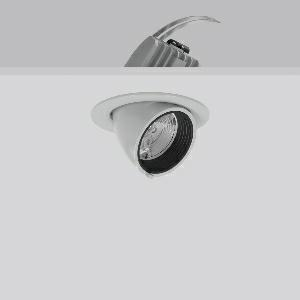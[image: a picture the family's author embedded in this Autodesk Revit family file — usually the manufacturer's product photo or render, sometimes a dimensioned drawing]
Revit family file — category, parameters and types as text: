
# Revit family: golas_mini_911573_004_76_199d
name_source: partatom
category: Lighting Fixtures
units: mm (PartAtom-declared; Revit-internal decimal feet)

## family parameters
Cut with Voids When Loaded = No
Host = Face
Light Source = No
Part Type = Normal
Room Calculation Point = No
Round Connector Dimension = Use Diameter
Shared = No

## types (1)
- GOLAS mini (1 x LED Modul 930, 1950 lm, 3000)
    Apparent Load = 20 VA
    Approval mark = CE
    CIE Flux Codes = 95 100 100 100 100
    Color Rendering = 90
    Color Temperature = 3000
    Default Elevation = 1800 mm
    Description = Series: GOLAS mini
Recessed LED projector for illuminating points to be highlighted. Housing: die-cast aluminium, powder-coated. 356° rotation range and 90° swivel range. Black plastic ring and recessed LED to prevent glare from the side. Optical assembly with lens made of plastic (polycarbonate) for the best homogeneous light distribution - can be changed without tools. Best colour rendering index Ra>90. Suitable for Recessed ceiling mounting. Installation without tools thanks to spring fastening system. Including separate LED converter with connecting cable 600 mm.High quality converter without flickering and stroboscopic effect. Through-wiring box (5 pole) available as accessory. The following accessories can be mounted without use of tools: interchangeable lenses, decorative glasses, honeycomb louvre, clear and frosted diffusers, white interchangeable plastic ring. 
Colour: silver
Diameter: 143 mm
Height: 3 mm
Cut-out diameter: 133 mm
Recess height: 170 mm
Luminaire: recess height: 115 mm
Lamp: LED
Socket: without socket
Colour temperature: 3000K
Colour rendering index (CRI): 92
System power: 20 W
Rated luminous flux: 1950 lm
Luminous efficiency: 98 lm/W
Control gear: Converter, dimmable, DALI
Protection class: II
Type of protection: IP 20
    Height = 0 mm  [stored 0 ft]
    Lamp = 1 x LED Modul 930
    Lamp Light Flux = 1950 lm
    Lamp count = 1
    Length = 143 mm
    Lifetime = 50000 h
    Luminous efficacy = 98 lm/W
    Manufacturer = RZB
    ModVariant = No
    Model = 911573.004.76
    Mounting Place = Ceiling, Wall
    Mounting Type = Recessed
    Number of Poles = 1
    OnlyDefault = Yes
    Power Factor = 1
    Product Name = GOLAS mini
    Product group = Recessed projectors
    ProductGroupID = 401
    Protection Class = Protection class II
    Protection Degree = IP 20
    RLX_Detail_Level = 1
    RLX_Emergency_Light_Flux = 0 lm
    RLX_Emergency_Type = 0
    RLX_Emergency_Type_DB = No
    RlxData = <blob elided: 53413 chars, md5=85e48752>
    Socket = socket
    Standby Power = 0 W
    System Light Flux = 1950 lm
    System Power = 20 W
    Type Comments = Product without accessories
    Type Image = 911438.004.jpg
    URL = http://relux.com
    VarID = ---
    Voltage = 230 V
    Voltage Range = 220-240 V
    Weight = 0.00 kg
    Width = 0 mm  [stored 0 ft]

note: [stored X ft] marks values corroborated as IEEE doubles in the binary element streams (Revit-internal decimal feet)

## geometry (parser evidence)
native form markers: Blend x4, Sweep x14
no freeform markers — native parametric forms only
